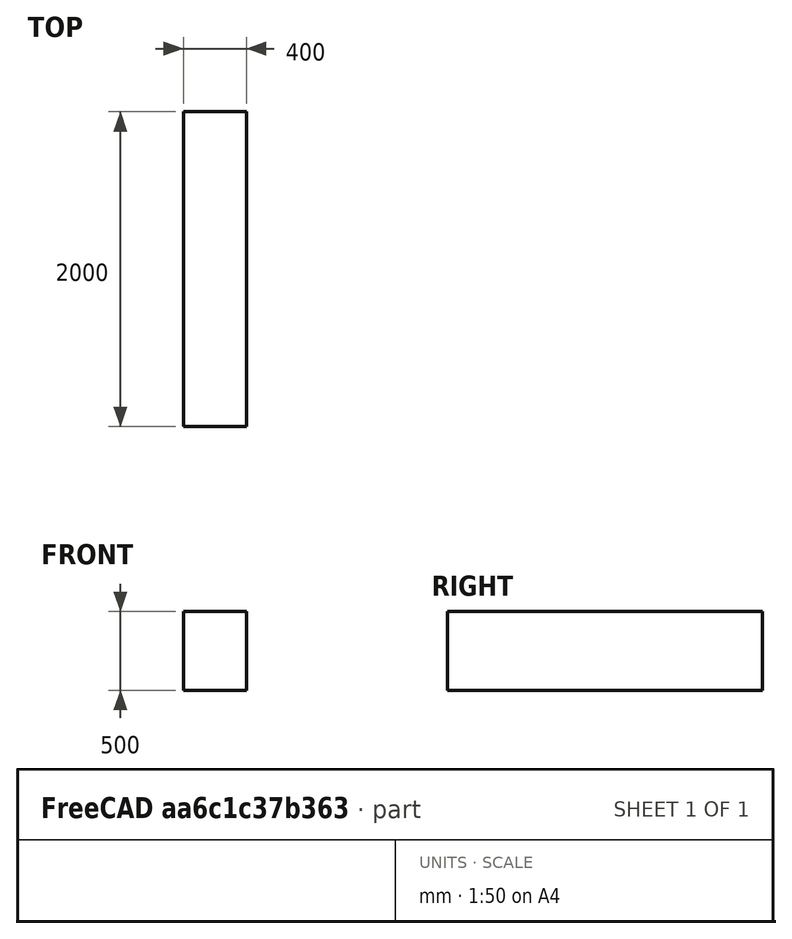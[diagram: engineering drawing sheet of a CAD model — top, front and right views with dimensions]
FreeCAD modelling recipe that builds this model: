
FCSTD DOCUMENT  (FreeCAD 1.0R39109 (Git))
Label: rectangular
License: All rights reserved
LicenseURL: http://en.wikipedia.org/wiki/All_rights_reserved
objects: Sketcher::SketchObject×1, PartDesign::Pad×1, PartDesign::Body×1
note: 6 computed .brp shape members not serialized (recipe doc carries the construction recipe); baked Part::Feature solids carry a one-line shape summary decoded from their .brp

FEATURE [Sketcher::SketchObject] Sketch
  ArcFitTolerance = 1e-06
  FullyConstrained = true
  MakeInternals = false
  Placement = pos=(0,0,0) rot=(1,0,0;1.5708rad)
  sketch-geometry (5):
    g0: LineSegment StartX=200 StartY=-250 StartZ=0 EndX=200 EndY=250 EndZ=0
    g1: LineSegment StartX=200 StartY=250 StartZ=0 EndX=-200 EndY=250 EndZ=0
    g2: LineSegment StartX=-200 StartY=250 StartZ=0 EndX=-200 EndY=-250 EndZ=0
    g3: LineSegment StartX=-200 StartY=-250 StartZ=0 EndX=200 EndY=-250 EndZ=0
    g4: GeomPoint [constr] X=0 Y=0 Z=0
  constraints (12):
    c: Coincident(g0,g1)
    c: Coincident(g1,g2)
    c: Coincident(g2,g3)
    c: Coincident(g3,g0)
    c: Vertical(g0)
    c: Vertical(g2)
    c: Horizontal(g1)
    c: Horizontal(g3)
    c: Symmetric(g2,g0,g4)
    c: Coincident(g4,g-1)
    c: DistanceX(g1,g1) = 400  'width'
    c: DistanceY(g2,g2) = 500  'depth'
FEATURE [PartDesign::Pad] Pad  label="length"
  Direction = (0,-1,-2e-16)
  Length = 2000
  Length2 = 10
  Placement = pos=(0,0,0) rot=(1,0,0;1.5708rad)
  Profile = -> Sketch
  ReferenceAxis = -> Sketch [N_Axis]
  Reversed = true
  Suppressed = false
  Type = 0
FEATURE [PartDesign::Body] Body  label="beam"
  AllowCompound = false
  Group = -> [Sketch,Pad]
  Origin = -> Origin
  Tip = -> Pad
  cross_section = Rectangular
